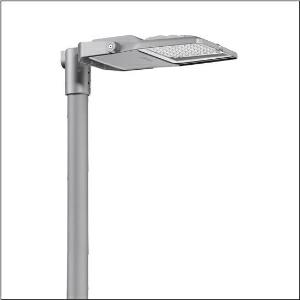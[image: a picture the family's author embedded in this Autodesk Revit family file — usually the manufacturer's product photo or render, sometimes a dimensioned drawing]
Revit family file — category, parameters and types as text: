
# Revit family: floodlight_fl_21_mini___pl43_5xa7775c2a3a_cdc0
name_source: partatom
category: Lighting Fixtures
units: mm (PartAtom-declared; Revit-internal decimal feet)

## family parameters
Cut with Voids When Loaded = No
Host = Face
Light Source = No
Part Type = Normal
Room Calculation Point = No
Round Connector Dimension = Use Diameter
Shared = No

## types (1)
- --- (1 x LED, 12500 lm, 89 W, 3000K)
    Apparent Load = 89 VA
    CIE Flux Codes = 27 78 99 100 100
    Color Rendering = 70
    Color Temperature = 3000K
    Default Elevation = 1800 mm
    Description = Floodlight FL 21 mini, floodlight, primary light control with lens, of PMMA, primary optical cover: protective disc, of toughened safety glass, transparent, light distribution: PL43, light emission: direct distribution, installation type: surface-mounted, LED, High Power LED, rated luminous flux: 12.500lm, luminous efficacy: 140lm/W, light colour: 730, colour temperature: 3000K, control: flexible luminous flux parameterisation, time-dependent luminous flux control, constant luminous flux control, overheat protection, pre-setting: logarithmic dimming characteristic, with terminal, 6-pole, mains connection: 220..240V, AC, 50/60Hz, start of lifetime: 89W, end of service life: 94W, reduction: 43W, luminaire housing, of diecast aluminium, powder-coated, Siteco® metallic grey (DB 702S), corrosivity category C5 mid according to DIN EN ISO 12944, sealing non-destructively replaceable, please order mast flange separately, mast bracket, of steel, galvanised, powder-coated, Siteco® metallic grey (DB 702S), Smart Interface above, protection rating (complete): IP66, insulation class (complete): insulation class II (safety insulation), certification: CE, ENEC, VDE, protection symbol: D, impact resistance: IK08, permissible operating ambient temperature: -40..+40°C, permissible operating ambient temperature for outdoor applications: -40..+50°C, standard: DIN EN 12944, LABS conformity tested according to VDMA 24364:2018-05, packaging unit: 1 piece

Light Distribution: PL43
    Height = 70 mm
    Lamp = 1 x LED
    Lamp Light Flux = 12500 lm
    Lamp Power = 89 W
    Lamp count = 1
    Length = 485 mm
    Luminous efficacy = 140 lm/W
    Manufacturer = Siteco
    ModVariant = No
    Model = 5XA7775C2A3A
    Number of Poles = 1
    OnlyDefault = Yes
    Power Factor = 1
    Product Name = Floodlight FL 21 mini | PL43
    Product group = floodlight | pylon annexe
    ProductGroupID = 6200
    Protection Class = Protection class II
    Protection Degree = IP 66
    RLX_Detail_Level = 1
    RLX_Emergency_Light_Flux = 0 lm
    RLX_Emergency_Type = 0
    RLX_Emergency_Type_DB = No
    RlxData = <blob elided: 100781 chars, md5=e4a03ada>
    Socket = socket
    Standby Power = 0 W
    System Light Flux = 12500 lm
    System Power = 89 W
    Type Comments = factory setting: luminous flux: 100 % | dim-lin: 254 | 456 mA
    Type Image = l_1007125.jpg
    URL = http://relux.com
    VarID = @adj_131461
    Voltage = 0 V
    Weight = 0.00 kg
    Width = 337 mm

## geometry (parser evidence)
native form markers: Blend x4, Sweep x12
no freeform markers — native parametric forms only
